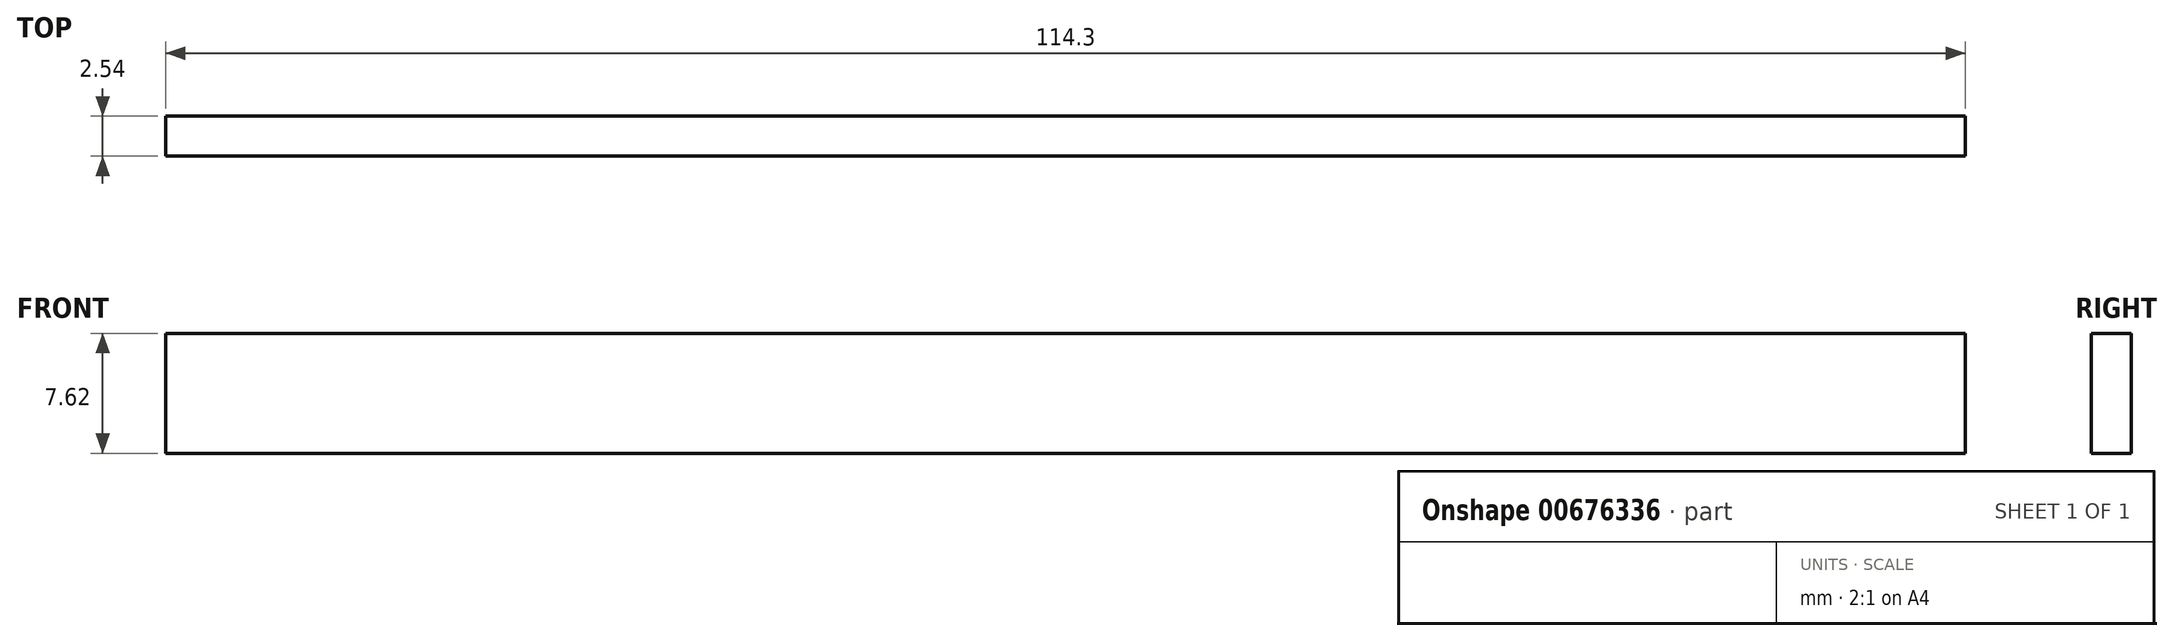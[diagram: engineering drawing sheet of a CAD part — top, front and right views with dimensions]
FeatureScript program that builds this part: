
annotation { "Feature Type Name" : "Feature", "Feature Type Description" : "" }
export const myFeature = defineFeature(function(context is Context, id is Id, definition is map)
    precondition{}
    {
        {
            var Q0;
            Q0=qCreatedBy(makeId("Front.planeOp"),FACE);
            var sketch = newSketch(context, id + "F0", { "sketchPlane" : qUnion([Q0])});
            skLineSegment(sketch, "E0.bottom", {"start": v(-57.15, -3.81) * mm, "end": v(57.15, -3.81) * mm});
            skLineSegment(sketch, "E0.top", {"start": v(-57.15, 3.81) * mm, "end": v(57.15, 3.81) * mm});
            skLineSegment(sketch, "E0.left", {"start": v(-57.15, -3.81) * mm, "end": v(-57.15, 3.81) * mm});
            skLineSegment(sketch, "E0.right", {"start": v(57.15, -3.81) * mm, "end": v(57.15, 3.81) * mm});
            skPoint(sketch, "E0.middle", {"position": v(0, 0) * mm});
            skSolve(sketch);
        }
        {
            var Q0;
            Q0 = qSketchRegion(id + "F0", true);
            extrude(context, id + "F1", {"entities" : qUnion([Q0]), "depth" : 2.54 * mm, "offsetDistance" : 25.4 * mm});
        }
    });
